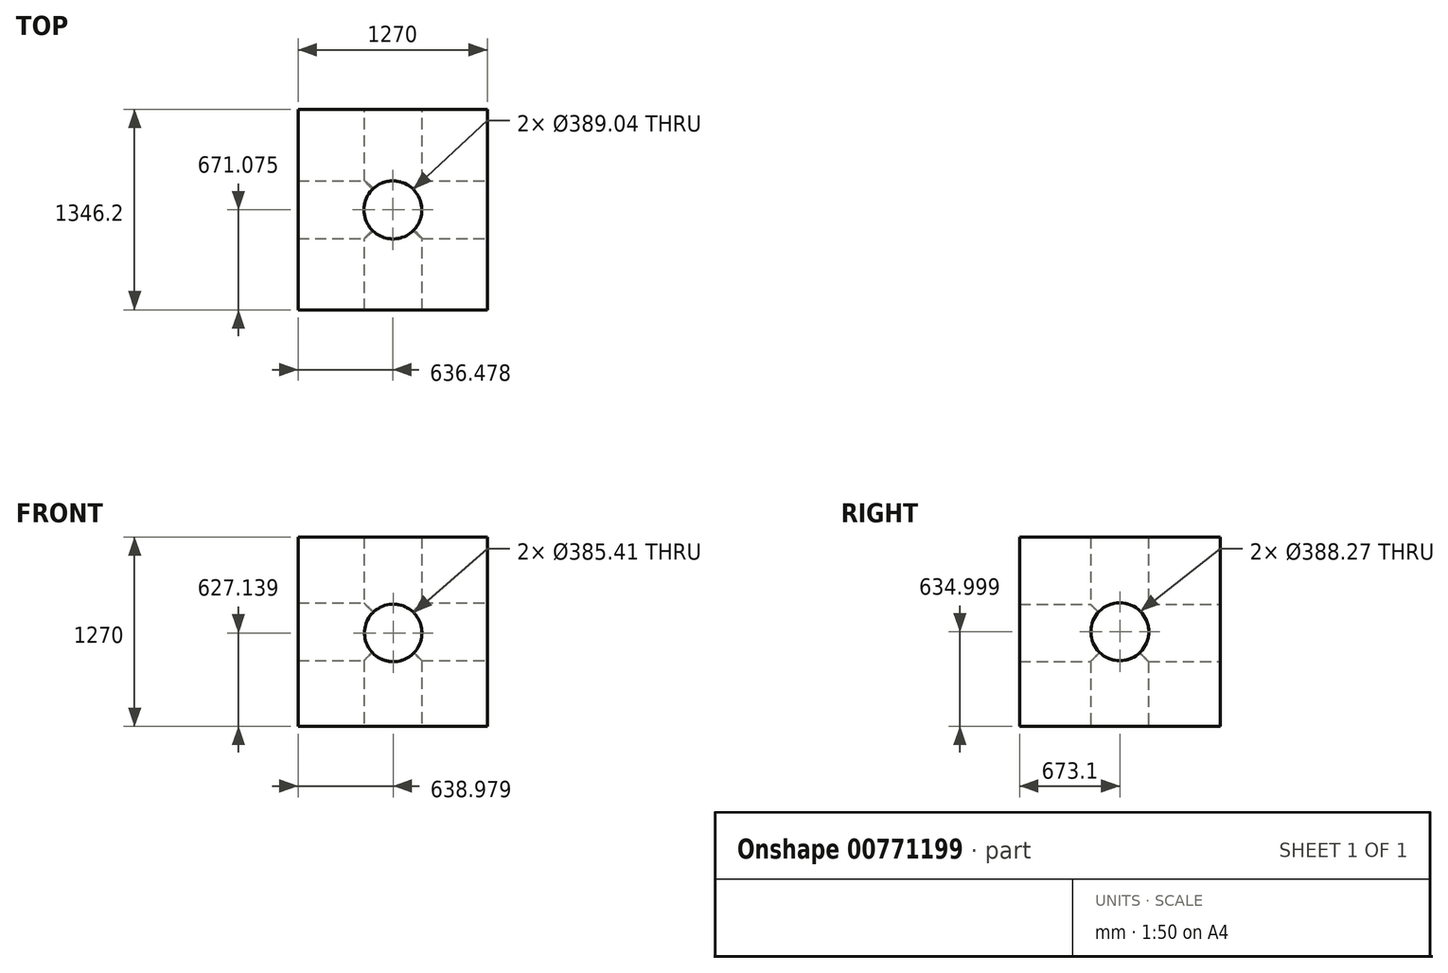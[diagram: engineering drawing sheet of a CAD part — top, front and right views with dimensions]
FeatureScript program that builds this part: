
annotation { "Feature Type Name" : "Feature", "Feature Type Description" : "" }
export const myFeature = defineFeature(function(context is Context, id is Id, definition is map)
    precondition{}
    {
        {
            var Q0;
            Q0=qCreatedBy(makeId("Front.planeOp"),FACE);
            var sketch = newSketch(context, id + "F0", { "sketchPlane" : qUnion([Q0])});
            skLineSegment(sketch, "E0.bottom", {"start": v(-52.99, 1250.98) * mm, "end": v(1217.01, 1250.98) * mm});
            skLineSegment(sketch, "E0.top", {"start": v(-52.99, -19.02) * mm, "end": v(1217.01, -19.02) * mm});
            skLineSegment(sketch, "E0.left", {"start": v(-52.99, 1250.98) * mm, "end": v(-52.99, -19.02) * mm});
            skLineSegment(sketch, "E0.right", {"start": v(1217.01, 1250.98) * mm, "end": v(1217.01, -19.02) * mm});
            skSolve(sketch);
        }
        {
            var Q0;
            Q0=makeQuery(id+"F0.imprint","IMPRINT",FACE,{"disambiguationData":[TD([[makeQuery(id+"F0.imprint","IMPRINT",EDGE,{"derivedFrom":sQuery(id+"F0.wireOp",EDGE,"E0.bottom")}),-1.0]])]});
            extrude(context, id + "F1", {"entities" : qUnion([Q0]), "depth" : 76.2 * mm, "offsetDistance" : 25.4 * mm});
        }
        {
            var Q0;
            Q0=makeQuery(id+"F1.opExtrude","CAP_FACE",FACE,{"disambiguationData":[OSD([sQuery(id+"F0.wireOp",EDGE,"E0.bottom"),sQuery(id+"F0.wireOp",EDGE,"E0.top"),sQuery(id+"F0.wireOp",EDGE,"E0.left"),sQuery(id+"F0.wireOp",EDGE,"E0.right")])],"isStart":true});
            var Q1;
            Q1=makeQuery(id+"F1.opExtrude","CAP_FACE",FACE,{"disambiguationData":[OSD([sQuery(id+"F0.wireOp",EDGE,"E0.bottom"),sQuery(id+"F0.wireOp",EDGE,"E0.top"),sQuery(id+"F0.wireOp",EDGE,"E0.left"),sQuery(id+"F0.wireOp",EDGE,"E0.right")])],"isStart":false});
            extrude(context, id + "F2", {"entities" : qUnion([Q0, Q1]), "operationType" : NewBodyOperationType.ADD, "depth" : 1270 * mm, "offsetDistance" : 25.4 * mm});
        }
        {
            var Q0;
            {var subQ0=sQuery(id+"F0.wireOp",EDGE,"E0.right");Q0=makeQuery(id+"F2.boolean.opBoolean","MERGE",FACE,{"derivedFrom":[makeQuery(id+"F1.opExtrude","SWEPT_FACE",FACE,{"disambiguationData":[OSD([subQ0])]}),makeQuery(id+"F2.opExtrude","SWEPT_FACE",FACE,{"disambiguationData":[OSD([subQ0]),TDD([makeQuery(id+"F1.opExtrude","CAP_EDGE",EDGE,{"disambiguationData":[OSD([subQ0])],"isStart":true})])]}),makeQuery(id+"F2.opExtrude","SWEPT_FACE",FACE,{"disambiguationData":[OSD([subQ0]),TDD([makeQuery(id+"F1.opExtrude","CAP_EDGE",EDGE,{"disambiguationData":[OSD([subQ0])],"isStart":false})])]})]});}
            var sketch = newSketch(context, id + "F3", { "sketchPlane" : qUnion([Q0])});
            skCircle(sketch, "E1", {"center": v(596.9, 615.98) * mm, "radius": 194.14 * mm});
            skPoint(sketch, "E1.centerSnap0", {"position": v(1270, 615.98) * mm});
            skPoint(sketch, "E1.centerSnap1", {"position": v(596.9, 1250.98) * mm});
            skSolve(sketch);
        }
        {
            var Q0;
            Q0=makeQuery(id+"F3.imprint","IMPRINT",FACE,{"disambiguationData":[TD([[makeQuery(id+"F3.imprint","IMPRINT",EDGE,{"derivedFrom":sQuery(id+"F3.wireOp",EDGE,"E1")}),1.0]])]});
            extrude(context, id + "F4", {"entities" : qUnion([Q0]), "operationType" : NewBodyOperationType.ADD, "depth" : 40.64 * mm, "offsetDistance" : 25.4 * mm});
        }
        {
            var Q0;
            Q0=makeQuery(id+"F4.opExtrude","CAP_FACE",FACE,{"disambiguationData":[OSD([sQuery(id+"F3.wireOp",EDGE,"E1")])],"isStart":false});
            extrude(context, id + "F5", {"entities" : qUnion([Q0]), "operationType" : NewBodyOperationType.REMOVE, "oppositeDirection" : true, "depth" : 1397 * mm, "offsetDistance" : 25.4 * mm});
        }
        {
            var Q0;
            {var subQ0=sQuery(id+"F0.wireOp",EDGE,"E0.right");var subQ1=sQuery(id+"F0.wireOp",EDGE,"E0.left");var subQ2=sQuery(id+"F0.wireOp",EDGE,"E0.top");var subQ3=sQuery(id+"F0.wireOp",EDGE,"E0.bottom");Q0=makeQuery(id+"F2.opExtrude","CAP_FACE",FACE,{"disambiguationData":[OSD([subQ3,subQ2,subQ1,subQ0]),TDD([makeQuery(id+"F1.opExtrude","CAP_FACE",FACE,{"disambiguationData":[OSD([subQ3,subQ2,subQ1,subQ0])],"isStart":true})])],"isStart":false});}
            var sketch = newSketch(context, id + "F6", { "sketchPlane" : qUnion([Q0])});
            skCircle(sketch, "E2", {"center": v(-585.99, 608.12) * mm, "radius": 192.7 * mm});
            skSolve(sketch);
        }
        {
            var Q0;
            Q0=makeQuery(id+"F6.imprint","IMPRINT",FACE,{"disambiguationData":[TD([[makeQuery(id+"F6.imprint","IMPRINT",EDGE,{"derivedFrom":sQuery(id+"F6.wireOp",EDGE,"E2")}),1.0]])]});
            extrude(context, id + "F7", {"entities" : qUnion([Q0]), "operationType" : NewBodyOperationType.REMOVE, "oppositeDirection" : true, "depth" : 2057.4 * mm, "offsetDistance" : 25.4 * mm});
        }
        {
            var Q0;
            {var subQ0=sQuery(id+"F0.wireOp",EDGE,"E0.top");Q0=makeQuery(id+"F2.boolean.opBoolean","MERGE",FACE,{"derivedFrom":[makeQuery(id+"F1.opExtrude","SWEPT_FACE",FACE,{"disambiguationData":[OSD([subQ0])]}),makeQuery(id+"F2.opExtrude","SWEPT_FACE",FACE,{"disambiguationData":[OSD([subQ0]),TDD([makeQuery(id+"F1.opExtrude","CAP_EDGE",EDGE,{"disambiguationData":[OSD([subQ0])],"isStart":true})])]}),makeQuery(id+"F2.opExtrude","SWEPT_FACE",FACE,{"disambiguationData":[OSD([subQ0]),TDD([makeQuery(id+"F1.opExtrude","CAP_EDGE",EDGE,{"disambiguationData":[OSD([subQ0])],"isStart":false})])]})]});}
            var sketch = newSketch(context, id + "F8", { "sketchPlane" : qUnion([Q0])});
            skCircle(sketch, "E3", {"center": v(583.49, -594.88) * mm, "radius": 194.52 * mm});
            skSolve(sketch);
        }
        {
            var Q0;
            Q0=makeQuery(id+"F8.imprint","IMPRINT",FACE,{"disambiguationData":[TD([[makeQuery(id+"F8.imprint","IMPRINT",EDGE,{"derivedFrom":sQuery(id+"F8.wireOp",EDGE,"E3")}),1.0]])]});
            extrude(context, id + "F9", {"entities" : qUnion([Q0]), "operationType" : NewBodyOperationType.REMOVE, "oppositeDirection" : true, "depth" : 1717.04 * mm, "offsetDistance" : 25.4 * mm});
        }
    });
